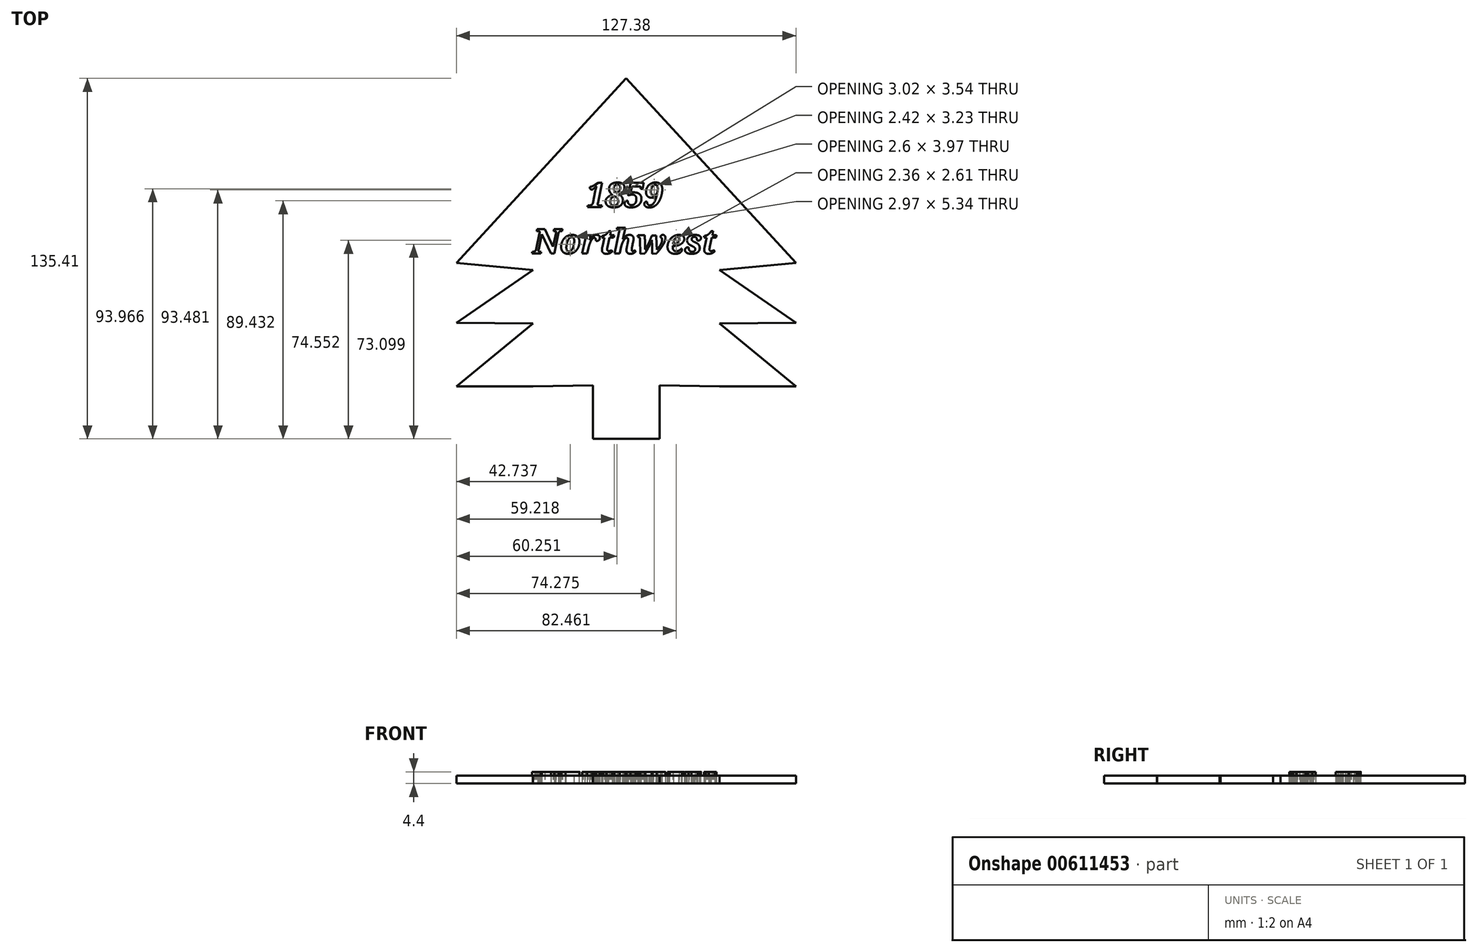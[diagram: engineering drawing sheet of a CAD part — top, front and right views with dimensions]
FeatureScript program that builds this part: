
annotation { "Feature Type Name" : "Feature", "Feature Type Description" : "" }
export const myFeature = defineFeature(function(context is Context, id is Id, definition is map)
    precondition{}
    {
        {
            var Q0;
            Q0=qCreatedBy(makeId("Top.planeOp"),FACE);
            var sketch = newSketch(context, id + "F0", { "sketchPlane" : qUnion([Q0])});
            skText(sketch, "E0", { "text": "      1859\nNorthwest", "fontName": "NotoSerif-BoldItalic.ttf"});
            const initialGuessF0  = {"E0": [-0.035, 0.0209, 1, 0, 0.00922]};
            skSetInitialGuess(sketch, initialGuessF0);
            skSolve(sketch);
        }
        {
            var Q0;
            Q0=qCreatedBy(makeId("Top.planeOp"),FACE);
            var sketch = newSketch(context, id + "F1", { "sketchPlane" : qUnion([Q0])});
            skLineSegment(sketch, "E1", {"start": v(0, 69.26) * mm, "end": v(-63.69, 0) * mm});
            skLineSegment(sketch, "E2", {"start": v(-63.69, 0) * mm, "end": v(-35, -2.7) * mm});
            skLineSegment(sketch, "E3", {"start": v(-35, -2.7) * mm, "end": v(-63.69, -22.5) * mm});
            skLineSegment(sketch, "E4", {"start": v(-63.69, -22.5) * mm, "end": v(-35, -22.83) * mm});
            skLineSegment(sketch, "E5", {"start": v(-35, -22.83) * mm, "end": v(-63.69, -46.36) * mm});
            skLineSegment(sketch, "E6", {"start": v(-63.69, -46.36) * mm, "end": v(-35, -46.37) * mm});
            skLineSegment(sketch, "E7", {"start": v(-35, -46.37) * mm, "end": v(-12.5, -46.07) * mm});
            skLineSegment(sketch, "E8", {"start": v(-12.5, -46.07) * mm, "end": v(-12.5, -66.15) * mm});
            skLineSegment(sketch, "E9", {"start": v(-12.5, -66.15) * mm, "end": v(0, -66.15) * mm});
            skLineSegment(sketch, "E10", {"start": v(0, 69.26) * mm, "end": v(0, -88.24) * mm, "construction": true});
            skLineSegment(sketch, "E11.MirrorCS", {"start": v(35, -2.7) * mm, "end": v(63.69, -22.5) * mm});
            skLineSegment(sketch, "E12.MirrorCS", {"start": v(12.5, -46.07) * mm, "end": v(12.5, -66.15) * mm});
            skLineSegment(sketch, "E13.MirrorCS", {"start": v(35, -22.83) * mm, "end": v(63.69, -46.36) * mm});
            skLineSegment(sketch, "E14.MirrorCS", {"start": v(63.69, -46.36) * mm, "end": v(35, -46.37) * mm});
            skLineSegment(sketch, "E15.MirrorCS", {"start": v(35, -46.37) * mm, "end": v(12.5, -46.07) * mm});
            skLineSegment(sketch, "E16.MirrorCS", {"start": v(63.69, 0) * mm, "end": v(35, -2.7) * mm});
            skLineSegment(sketch, "E17.MirrorCS", {"start": v(63.69, -22.5) * mm, "end": v(35, -22.83) * mm});
            skLineSegment(sketch, "E18.MirrorCS", {"start": v(0, 69.26) * mm, "end": v(63.69, 0) * mm});
            skLineSegment(sketch, "E19.MirrorCS", {"start": v(12.5, -66.15) * mm, "end": v(0, -66.15) * mm});
            skSolve(sketch);
        }
        {
            var Q0;
            Q0 = qSketchRegion(id + "F0", true);
            var Q1;
            Q1 = qConstructionFilter(qBodyType(qCreatedBy(id + "F0" ,EDGE), BodyType.WIRE), ConstructionObject.NO);
            extrude(context, id + "F2", {"entities" : qUnion([Q0]), "surfaceEntities" : qUnion([Q1]), "depth" : 4.4 * mm, "offsetDistance" : 25 * mm});
        }
        {
            var Q0;
            Q0 = qSketchRegion(id + "F1", true);
            extrude(context, id + "F3", {"entities" : qUnion([Q0]), "depth" : 3 * mm, "offsetDistance" : 25 * mm});
        }
    });
